# Revit family: Door single swing
name_source: partatom
category: Doors
revit_build: Autodesk Revit 2016 (Build: 20160314_0715(x64)
units: mm (PartAtom-declared; Revit-internal decimal feet)

## family parameters
Always vertical = Yes
Cut with Voids When Loaded = No
Host = Wall
OmniClass Number = 23.30.10.00
OmniClass Title = Doors
Room Calculation Point = No
Shared = No

## types (1)
- 1000 x 2080 mm - M10 x M21
    Analytic Construction = <None>
    BIMobject category = Doors
    Clear Opening 90° = 835 mm
    Depth = 0
    Description = Bering is an exterior door in the range Function. Here you find designes with inspiration from both the 1930s functionalism and the neo-functional style that we are experiencing today. The doors have many innovative solutions, including a unique glazing method with solid strips without seams or screws. Here in out-swing version.
    Design country = Sweden
    Door Panel Height = 2033 mm
    Door Panel Width = 937 mm  [stored 3.07415 ft]
    Edition number = 1
    Frame Depth = 105 mm  [stored 0.344488 ft]
    Frame Projection Ext. = 25 mm  [stored 0.082021 ft]
    Frame Projection Int. = 25 mm  [stored 0.082021 ft]
    Frame Width = 75 mm  [stored 0.246063 ft]
    Function = Exterior
    Heat Transfer Coefficient (U) = 0.9100 W/(m²·K)
    Height = 2080 mm  [stored 6.82415 ft]
    IFC Classification = Door
    Manufacturer = SWEDOOR JELD-WEN
    Manufacturer country = Sweden
    Manufacturer name = SWEDOOR JELD-WEN
    Material main = Wood
    Material secondary = Glass
    Model = Swedoor_JW_exterior_door_Function_Bering_single_outswing
    NBS Reference Code = 59-23
    NBS Reference Description = Doorsets
    Nominal height = 0
    Nominal width = 0
    Product Name = Function Door
    Product certification = http://www.swedoor.se
    Product data url = http://bimobject.com
    Product family = Exterior doors
    Product group = Function
    Rough Height = 2092 mm  [stored 6.86352 ft]
    Rough Width = 1024 mm  [stored 3.35958 ft]
    U-value = 0.91 W/(m²·K)
    UNSPSC Code = 301715
    Uniclass 1.4 Code = L411
    Uniclass 1.4 Description = Doors
    Uniclass 2.0 Code = PR-59-23
    Uniclass 2.0 Description = Doorsets
    Wall Closure = By host
    Weight Net (Kg) = 0
    Width = 1000 mm  [stored 3.28084 ft]

note: [stored X ft] marks values corroborated as IEEE doubles in the binary element streams (Revit-internal decimal feet)

## geometry (parser evidence)
native form markers: Blend x6, Sweep x11
no freeform markers — native parametric forms only
